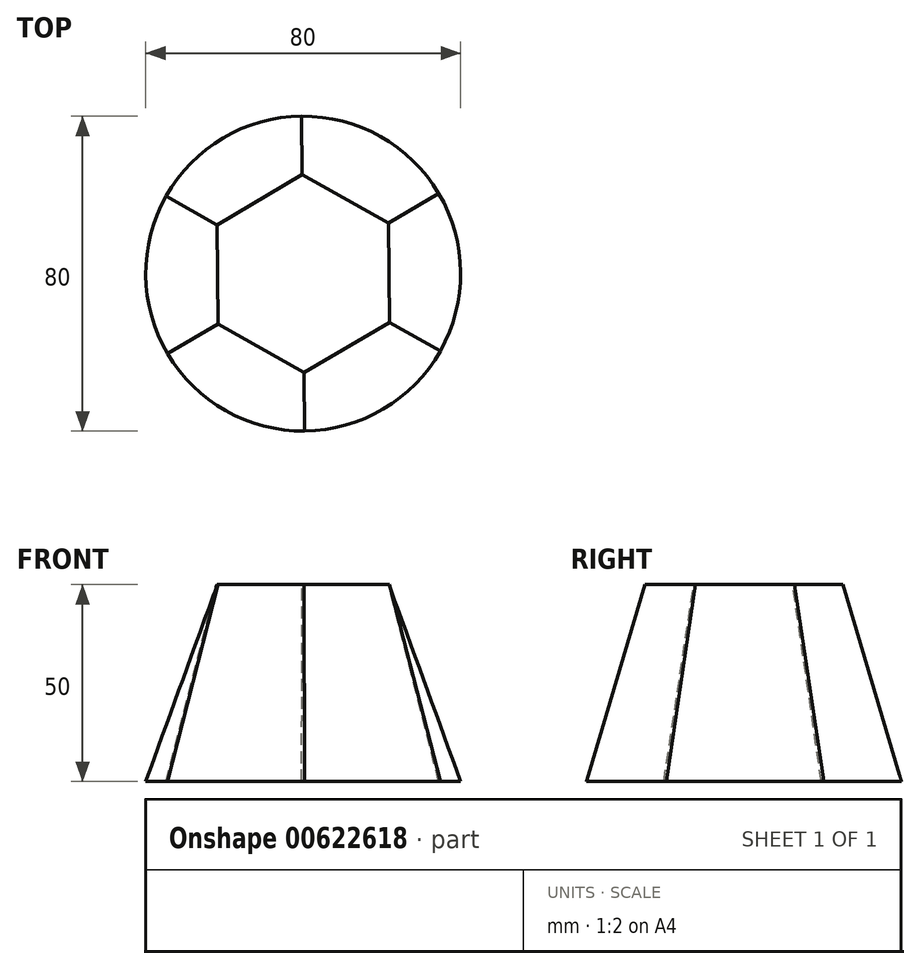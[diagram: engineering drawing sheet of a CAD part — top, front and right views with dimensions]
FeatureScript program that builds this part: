
annotation { "Feature Type Name" : "Feature", "Feature Type Description" : "" }
export const myFeature = defineFeature(function(context is Context, id is Id, definition is map)
    precondition{}
    {
        {
            var Q0;
            Q0=qCreatedBy(makeId("Top.planeOp"),FACE);
            var sketch = newSketch(context, id + "F0", { "sketchPlane" : qUnion([Q0])});
            skCircle(sketch, "E0", {"center": v(0, 0) * mm, "radius": 40 * mm});
            skSolve(sketch);
        }
        {
            var Q0;
            Q0=qCreatedBy(makeId("Top.planeOp"),FACE);
            cPlane(context, id + "F1", {"entities" : qUnion([Q0]), "cplaneType" : CPlaneType.OFFSET, "offset" : 50 * mm, "width" : 150 * mm, "height" : 150 * mm});
        }
        {
            var Q0;
            Q0=qCreatedBy(id+"F1.planeOp",FACE);
            var sketch = newSketch(context, id + "F2", { "sketchPlane" : qUnion([Q0])});
            skCircle(sketch, "E1.cCircle", {"center": v(0, 0) * mm, "radius": 21.8 * mm, "construction": true});
            skLineSegment(sketch, "E1.0", {"start": v(21.91, -12.37) * mm, "end": v(0.25, -25.16) * mm});
            skLineSegment(sketch, "E1.1", {"start": v(0.25, -25.16) * mm, "end": v(-21.67, -12.8) * mm});
            skLineSegment(sketch, "E1.2", {"start": v(-21.67, -12.8) * mm, "end": v(-21.91, 12.37) * mm});
            skLineSegment(sketch, "E1.3", {"start": v(-21.91, 12.37) * mm, "end": v(-0.25, 25.16) * mm});
            skLineSegment(sketch, "E1.4", {"start": v(-0.25, 25.16) * mm, "end": v(21.67, 12.8) * mm});
            skLineSegment(sketch, "E1.5", {"start": v(21.67, 12.8) * mm, "end": v(21.91, -12.37) * mm});
            skPoint(sketch, "E1.0.midPoint", {"position": v(11.08, -18.76) * mm});
            skSolve(sketch);
        }
        {
            var Q0;
            Q0=makeQuery(id+"F0.imprint","IMPRINT",FACE,{"disambiguationData":[TD([[makeQuery(id+"F0.imprint","IMPRINT",EDGE,{"derivedFrom":sQuery(id+"F0.wireOp",EDGE,"E0")}),1.0]])]});
            var Q1;
            Q1=makeQuery(id+"F2.imprint","IMPRINT",FACE,{"disambiguationData":[TD([[makeQuery(id+"F2.imprint","IMPRINT",EDGE,{"derivedFrom":sQuery(id+"F2.wireOp",EDGE,"E1.0")}),-1.0]])]});
            loft(context, id + "F3", {"sheetProfilesArray" : [{ "sheetProfileEntities" : qUnion([Q0]) }, { "sheetProfileEntities" : qUnion([Q1]) }]});
        }
    });
